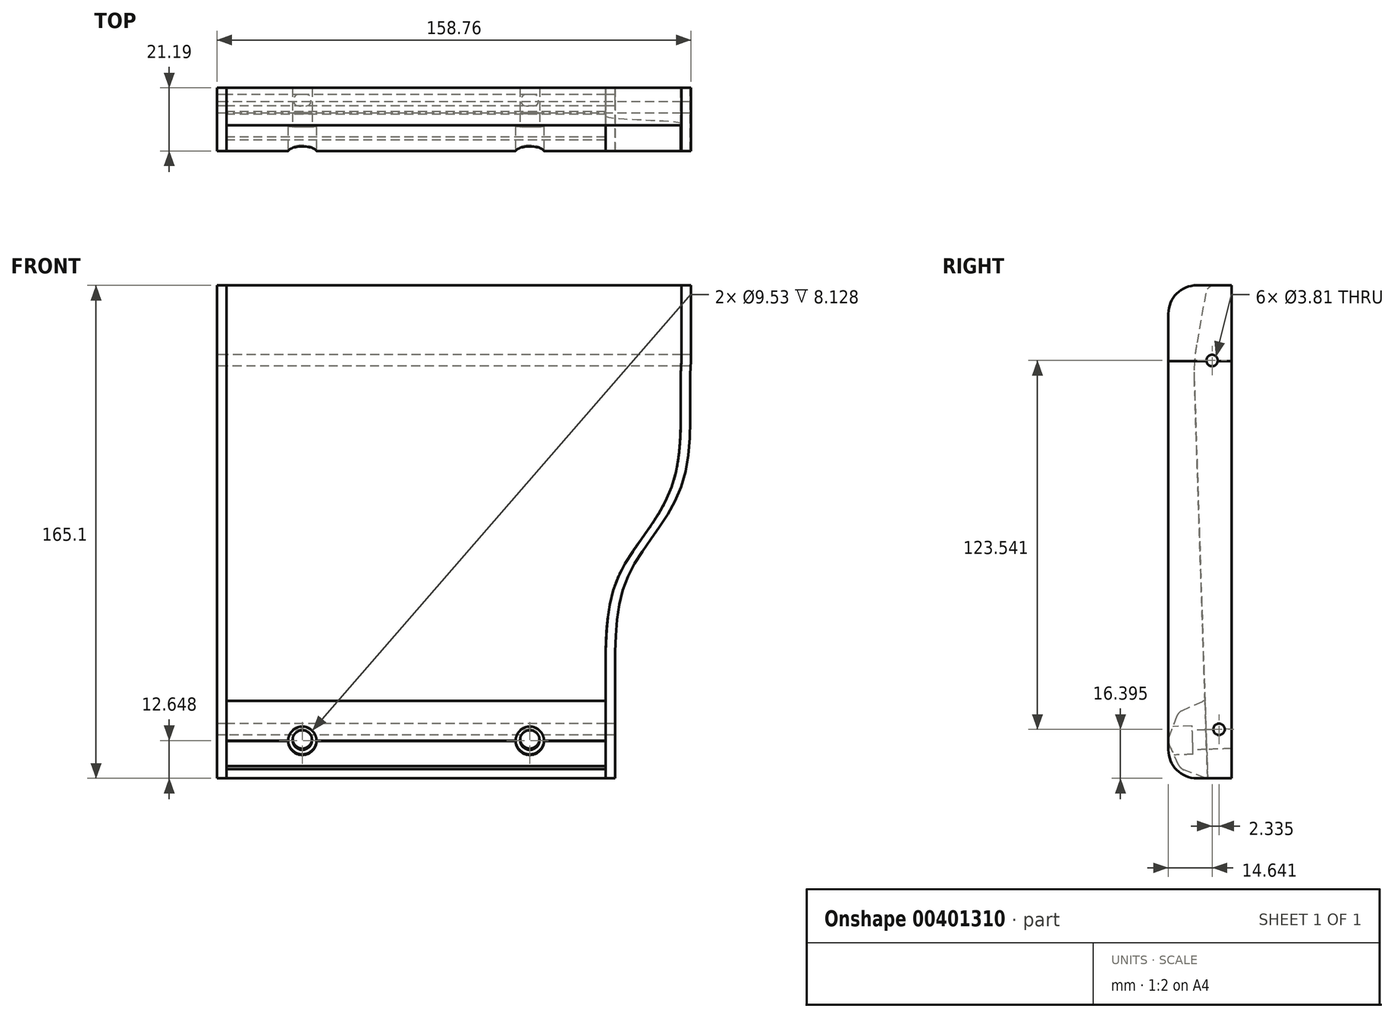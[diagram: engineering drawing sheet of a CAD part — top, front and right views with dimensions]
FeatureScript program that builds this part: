
annotation { "Feature Type Name" : "Feature", "Feature Type Description" : "" }
export const myFeature = defineFeature(function(context is Context, id is Id, definition is map)
    precondition{}
    {
        {
            var Q0;
            Q0=qCreatedBy(makeId("Front.planeOp"),FACE);
            var sketch = newSketch(context, id + "F0", { "sketchPlane" : qUnion([Q0])});
            skLineSegment(sketch, "E0", {"start": v(0, 165.1) * mm, "end": v(0, 0) * mm});
            skLineSegment(sketch, "E1", {"start": v(0, 165.1) * mm, "end": v(152.4, 165.1) * mm});
            skLineSegment(sketch, "E2", {"start": v(0, 0) * mm, "end": v(127, 0) * mm});
            skLineSegment(sketch, "E3", {"start": v(127, 0) * mm, "end": v(127, 25.4) * mm});
            skLineSegment(sketch, "E4", {"start": v(152.4, 165.1) * mm, "end": v(152.4, 139.7) * mm});
            skFitSpline(sketch, "E5", {"points": [v(152.4, 139.7) * mm, v(149.48, 98.62) * mm, v(130.97, 66.83) * mm, v(127, 25.4) * mm], "startDerivative": vector(-8.21, -91.05) * mm, "endDerivative": vector(-1.06, -132.64) * mm});
            skSolve(sketch);
        }
        {
            var Q0;
            Q0=makeQuery(id+"F0.imprint","IMPRINT",FACE,{"disambiguationData":[TD([[makeQuery(id+"F0.imprint","IMPRINT",EDGE,{"derivedFrom":sQuery(id+"F0.wireOp",EDGE,"E0")}),1.0]])]});
            extrude(context, id + "F1", {"entities" : qUnion([Q0]), "depth" : 12.7 * mm});
        }
        {
            var Q0;
            Q0=makeQuery(id+"F1.opExtrude","SWEPT_FACE",FACE,{"disambiguationData":[OSD([sQuery(id+"F0.wireOp",EDGE,"E0")])]});
            var sketch = newSketch(context, id + "F2", { "sketchPlane" : qUnion([Q0])});
            skLineSegment(sketch, "E6", {"start": v(8.67, 162.48) * mm, "end": v(11.76, 145.14) * mm});
            skLineSegment(sketch, "E7", {"start": v(12.52, 134.54) * mm, "end": v(8.06, 0) * mm});
            skLineSegment(sketch, "E8", {"start": v(5.54, 165.1) * mm, "end": v(0, 165.1) * mm, "construction": true});
            skLineSegment(sketch, "E9", {"start": v(0, 165.1) * mm, "end": v(0, 0) * mm, "construction": true});
            skLineSegment(sketch, "E10", {"start": v(0, 0) * mm, "end": v(8.06, 0) * mm, "construction": true});
            skPoint(sketch, "E11.visualSharp", {"position": v(12.7, 139.88) * mm});
            skArc(sketch, "E11.filletArc", {"start": v(12.52, 134.54) * mm, "mid": v(12.42, 139.86) * mm, "end": v(11.76, 145.14) * mm});
            skPoint(sketch, "E12.visualSharp", {"position": v(8.2, 165.1) * mm});
            skArc(sketch, "E12.filletArc", {"start": v(8.67, 162.48) * mm, "mid": v(7.58, 164.36) * mm, "end": v(5.54, 165.1) * mm});
            skLineSegment(sketch, "E13", {"start": v(5.54, 165.1) * mm, "end": v(12.7, 165.1) * mm});
            skLineSegment(sketch, "E14", {"start": v(12.7, 165.1) * mm, "end": v(12.7, 0) * mm});
            skLineSegment(sketch, "E15", {"start": v(12.7, 0) * mm, "end": v(8.06, 0) * mm});
            skSolve(sketch);
        }
        {
            var Q0;
            Q0 = qSketchRegion(id + "F2", true);
            var Q1;
            Q1=makeQuery(id+"F1.opExtrude","SWEPT_FACE",FACE,{"disambiguationData":[OSD([sQuery(id+"F0.wireOp",EDGE,"E4")])]});
            extrude(context, id + "F3", {"entities" : qUnion([Q0]), "operationType" : NewBodyOperationType.REMOVE, "endBound" : BoundingType.UP_TO_SURFACE, "oppositeDirection" : true, "endBoundEntityFace" : qUnion([Q1]), "depth" : 139.95 * mm});
        }
        {
            var Q0;
            Q0=makeQuery(id+"F1.opExtrude","SWEPT_FACE",FACE,{"disambiguationData":[OSD([sQuery(id+"F0.wireOp",EDGE,"E0")])]});
            var sketch = newSketch(context, id + "F4", { "sketchPlane" : qUnion([Q0])});
            skArc(sketch, "E16", {"start": v(8.06, 0) * mm, "mid": v(21.2, 12.7) * mm, "end": v(8.93, 26.24) * mm});
            skLineSegment(sketch, "E17", {"start": v(8.93, 26.24) * mm, "end": v(8.06, 0) * mm});
            skCircle(sketch, "E18.cCircle", {"center": v(8.2, 12.99) * mm, "radius": 13.26 * mm, "construction": true});
            skLineSegment(sketch, "E18.0", {"start": v(20.9, 11.35) * mm, "end": v(17.8, 4.5) * mm});
            skLineSegment(sketch, "E18.1", {"start": v(16.02, 2.84) * mm, "end": v(8.99, 0.2) * mm});
            skLineSegment(sketch, "E18.6", {"start": v(9.83, 25.7) * mm, "end": v(16.68, 22.6) * mm});
            skLineSegment(sketch, "E18.7", {"start": v(18.34, 20.82) * mm, "end": v(20.99, 13.78) * mm});
            skPoint(sketch, "E19.visualSharp", {"position": v(21.45, 12.55) * mm});
            skArc(sketch, "E19.filletArc", {"start": v(20.9, 11.35) * mm, "mid": v(21.19, 12.56) * mm, "end": v(20.99, 13.78) * mm});
            skPoint(sketch, "E20.visualSharp", {"position": v(17.26, 3.3) * mm});
            skArc(sketch, "E20.filletArc", {"start": v(16.02, 2.84) * mm, "mid": v(17.08, 3.5) * mm, "end": v(17.8, 4.5) * mm});
            skPoint(sketch, "E21.visualSharp", {"position": v(7.75, -0.27) * mm});
            skArc(sketch, "E21.filletArc", {"start": v(8.06, 0) * mm, "mid": v(8.53, 0.06) * mm, "end": v(8.99, 0.2) * mm});
            skPoint(sketch, "E22.visualSharp", {"position": v(17.88, 22.05) * mm});
            skArc(sketch, "E22.filletArc", {"start": v(18.34, 20.82) * mm, "mid": v(17.69, 21.87) * mm, "end": v(16.68, 22.6) * mm});
            skPoint(sketch, "E23.visualSharp", {"position": v(8.63, 26.24) * mm});
            skArc(sketch, "E23.filletArc", {"start": v(9.83, 25.7) * mm, "mid": v(9.39, 25.86) * mm, "end": v(8.92, 25.96) * mm});
            skLineSegment(sketch, "E24", {"start": v(21.45, 12.55) * mm, "end": v(-5.06, 13.43) * mm, "construction": true});
            skSolve(sketch);
        }
        {
            var Q0;
            {var subQ4=sQuery(id+"F4.wireOp",EDGE,"E18.0");Q0=makeQuery(id+"F4.imprint","IMPRINT",FACE,{"disambiguationData":[TD([[makeQuery(id+"F4.imprint","IMPRINT",EDGE,{"derivedFrom":subQ4}),-1.0]])]});}
            var Q1;
            Q1=makeQuery(id+"F1.opExtrude","SWEPT_FACE",FACE,{"disambiguationData":[OSD([sQuery(id+"F0.wireOp",EDGE,"E3")])]});
            extrude(context, id + "F5", {"entities" : qUnion([Q0]), "endBound" : BoundingType.UP_TO_SURFACE, "oppositeDirection" : true, "endBoundEntityFace" : qUnion([Q1]), "depth" : 36.55 * mm});
        }
        {
            var Q0;
            Q0=makeQuery(id+"F3.boolean.opBoolean","COPY",FACE,{"derivedFrom":makeQuery(id+"F3.opExtrude","SWEPT_FACE",FACE,{"disambiguationData":[OSD([sQuery(id+"F2.wireOp",EDGE,"E7")])]})});
            cPlane(context, id + "F6", {"entities" : qUnion([Q0]), "cplaneType" : CPlaneType.OFFSET, "offset" : 12.7 * mm, "width" : 152.4 * mm, "height" : 152.4 * mm});
        }
        {
            var Q0;
            Q0=qCreatedBy(id+"F6.planeOp",FACE);
            var sketch = newSketch(context, id + "F7", { "sketchPlane" : qUnion([Q0])});
            skPoint(sketch, "E25.0", {"position": v(0, 13.2) * mm});
            skLineSegment(sketch, "E26", {"start": v(0, 13.2) * mm, "end": v(195.68, 13.2) * mm, "construction": true});
            skCircle(sketch, "E27", {"center": v(25.4, 13.2) * mm, "radius": 4.76 * mm});
            skCircle(sketch, "E28", {"center": v(101.6, 13.2) * mm, "radius": 4.76 * mm});
            skCircle(sketch, "E29", {"center": v(25.4, 13.2) * mm, "radius": 3.26 * mm});
            skCircle(sketch, "E30", {"center": v(101.6, 13.2) * mm, "radius": 3.26 * mm});
            skSolve(sketch);
        }
        {
            var Q0;
            Q0=makeQuery(id+"F7.imprint","IMPRINT",FACE,{"disambiguationData":[TD([[makeQuery(id+"F7.imprint","IMPRINT",EDGE,{"derivedFrom":sQuery(id+"F7.wireOp",EDGE,"E29")}),1.0]])]});
            var Q1;
            Q1=makeQuery(id+"F7.imprint","IMPRINT",FACE,{"disambiguationData":[TD([[makeQuery(id+"F7.imprint","IMPRINT",EDGE,{"derivedFrom":sQuery(id+"F7.wireOp",EDGE,"E30")}),1.0]])]});
            extrude(context, id + "F8", {"entities" : qUnion([Q0, Q1]), "operationType" : NewBodyOperationType.REMOVE, "endBound" : BoundingType.THROUGH_ALL, "oppositeDirection" : true, "depth" : 25.4 * mm});
        }
        {
            var Q0;
            Q0=makeQuery(id+"F7.imprint","IMPRINT",FACE,{"disambiguationData":[TD([[makeQuery(id+"F7.imprint","IMPRINT",EDGE,{"derivedFrom":sQuery(id+"F7.wireOp",EDGE,"E27")}),1.0]])]});
            var Q1;
            Q1=makeQuery(id+"F7.imprint","IMPRINT",FACE,{"disambiguationData":[TD([[makeQuery(id+"F7.imprint","IMPRINT",EDGE,{"derivedFrom":sQuery(id+"F7.wireOp",EDGE,"E28")}),1.0]])]});
            extrude(context, id + "F9", {"entities" : qUnion([Q0, Q1]), "operationType" : NewBodyOperationType.REMOVE, "oppositeDirection" : true, "depth" : 8.13 * mm});
        }
        {
            var Q0;
            Q0=makeQuery(id+"F1.opExtrude","SWEPT_FACE",FACE,{"disambiguationData":[OSD([sQuery(id+"F0.wireOp",EDGE,"E2")])]});
            var sketch = newSketch(context, id + "F10", { "sketchPlane" : qUnion([Q0])});
            skPoint(sketch, "E31.0", {"position": v(0, 21.18) * mm});
            skLineSegment(sketch, "E32.bottom", {"start": v(0, 0) * mm, "end": v(-3.17, 0) * mm});
            skLineSegment(sketch, "E32.top", {"start": v(0, 21.18) * mm, "end": v(-3.17, 21.18) * mm});
            skLineSegment(sketch, "E32.left", {"start": v(0, 0) * mm, "end": v(0, 21.18) * mm});
            skLineSegment(sketch, "E32.right", {"start": v(-3.17, 0) * mm, "end": v(-3.17, 21.18) * mm});
            skSolve(sketch);
        }
        {
            var Q0;
            {var subQ1=sQuery(id+"F0.wireOp",EDGE,"E2");var subQ2=makeQuery(id+"F1.opExtrude","CAP_EDGE",EDGE,{"disambiguationData":[OSD([subQ1])],"isStart":true});Q0=makeQuery(id+"F10.imprint","IMPRINT",FACE,{"disambiguationData":[TD([[makeQuery(id+"F10.imprint","IMPRINT",EDGE,{"derivedFrom":subQ2}),1.0]])]});}
            var sketch = newSketch(context, id + "F11", { "sketchPlane" : qUnion([Q0])});
            skPoint(sketch, "E33.0", {"position": v(127, 21.18) * mm});
            skPoint(sketch, "E34.0", {"position": v(127, 0) * mm});
            skLineSegment(sketch, "E35.bottom", {"start": v(127, 0) * mm, "end": v(130.18, 0) * mm});
            skLineSegment(sketch, "E35.top", {"start": v(127, 21.18) * mm, "end": v(130.18, 21.18) * mm});
            skLineSegment(sketch, "E35.left", {"start": v(127, 0) * mm, "end": v(127, 21.18) * mm});
            skLineSegment(sketch, "E35.right", {"start": v(130.18, 0) * mm, "end": v(130.18, 21.18) * mm});
            skSolve(sketch);
        }
        {
            var Q0;
            {var subQ1=sQuery(id+"F11.wireOp",EDGE,"E35.bottom");Q0=makeQuery(id+"F11.imprint","IMPRINT",FACE,{"disambiguationData":[TD([[makeQuery(id+"F11.imprint","IMPRINT",EDGE,{"derivedFrom":subQ1}),1.0]])]});}
            var Q1;
            Q1=makeQuery(id+"F1.opExtrude","CAP_EDGE",EDGE,{"disambiguationData":[OSD([sQuery(id+"F0.wireOp",EDGE,"E3")])],"isStart":true});
            var Q2;
            Q2=makeQuery(id+"F1.opExtrude","CAP_EDGE",EDGE,{"disambiguationData":[OSD([sQuery(id+"F0.wireOp",EDGE,"E5")])],"isStart":true});
            var Q3;
            Q3=makeQuery(id+"F1.opExtrude","CAP_EDGE",EDGE,{"disambiguationData":[OSD([sQuery(id+"F0.wireOp",EDGE,"E4")])],"isStart":true});
            sweep(context, id + "F12", {"profiles" : qUnion([Q0]), "path" : qUnion([Q1, Q2, Q3]), "keepProfileOrientation" : true});
        }
        {
            var Q0;
            Q0 = qSketchRegion(id + "F10", true);
            var Q1;
            Q1=makeQuery(id+"F1.opExtrude","CAP_EDGE",EDGE,{"disambiguationData":[OSD([sQuery(id+"F0.wireOp",EDGE,"E0")])],"isStart":true});
            sweep(context, id + "F13", {"profiles" : qUnion([Q0]), "path" : qUnion([Q1])});
        }
        {
            var Q0;
            Q0=makeQuery(id+"F13.opSweep","SWEPT_FACE",FACE,{"disambiguationData":[OSD([sQuery(id+"F0.wireOp",EDGE,"E0"),sQuery(id+"F10.wireOp",EDGE,"E32.right")])]});
            var sketch = newSketch(context, id + "F14", { "sketchPlane" : qUnion([Q0])});
            skPoint(sketch, "E36.visualSharp", {"position": v(21.18, 165.1) * mm});
            skArc(sketch, "E36.filletArc", {"start": v(21.18, 155.58) * mm, "mid": v(18.39, 162.31) * mm, "end": v(11.65, 165.1) * mm});
            skPoint(sketch, "E37.visualSharp", {"position": v(21.18, 0) * mm});
            skArc(sketch, "E37.filletArc", {"start": v(11.65, 0) * mm, "mid": v(18.39, 2.79) * mm, "end": v(21.18, 9.53) * mm});
            skLineSegment(sketch, "E38", {"start": v(11.65, 165.1) * mm, "end": v(21.18, 165.1) * mm});
            skLineSegment(sketch, "E39", {"start": v(21.18, 9.53) * mm, "end": v(21.18, 0) * mm});
            skSolve(sketch);
        }
        {
            var Q0;
            {var subQ0=sQuery(id+"F14.wireOp",EDGE,"E36.filletArc");Q0=makeQuery(id+"F14.imprint","IMPRINT",FACE,{"disambiguationData":[TD([[makeQuery(id+"F14.imprint","IMPRINT",EDGE,{"derivedFrom":subQ0}),-1.0]])]});}
            var Q1;
            {var subQ0=sQuery(id+"F14.wireOp",EDGE,"E37.filletArc");Q1=makeQuery(id+"F14.imprint","IMPRINT",FACE,{"disambiguationData":[TD([[makeQuery(id+"F14.imprint","IMPRINT",EDGE,{"derivedFrom":subQ0}),-1.0]])]});}
            extrude(context, id + "F15", {"entities" : qUnion([Q0, Q1]), "operationType" : NewBodyOperationType.REMOVE, "endBound" : BoundingType.THROUGH_ALL, "oppositeDirection" : true, "depth" : 25.4 * mm});
        }
        {
            var Q0;
            Q0=makeQuery(id+"F13.opSweep","SWEPT_FACE",FACE,{"disambiguationData":[OSD([sQuery(id+"F0.wireOp",EDGE,"E0"),sQuery(id+"F10.wireOp",EDGE,"E32.right")])]});
            var sketch = newSketch(context, id + "F16", { "sketchPlane" : qUnion([Q0])});
            skCircle(sketch, "E40", {"center": v(6.55, 139.94) * mm, "radius": 1.9 * mm});
            skCircle(sketch, "E41", {"center": v(4.21, 16.4) * mm, "radius": 1.9 * mm});
            skSolve(sketch);
        }
        {
            var Q0;
            Q0 = qSketchRegion(id + "F16", true);
            extrude(context, id + "F17", {"entities" : qUnion([Q0]), "operationType" : NewBodyOperationType.REMOVE, "endBound" : BoundingType.THROUGH_ALL, "oppositeDirection" : true, "depth" : 25.4 * mm});
        }
    });
